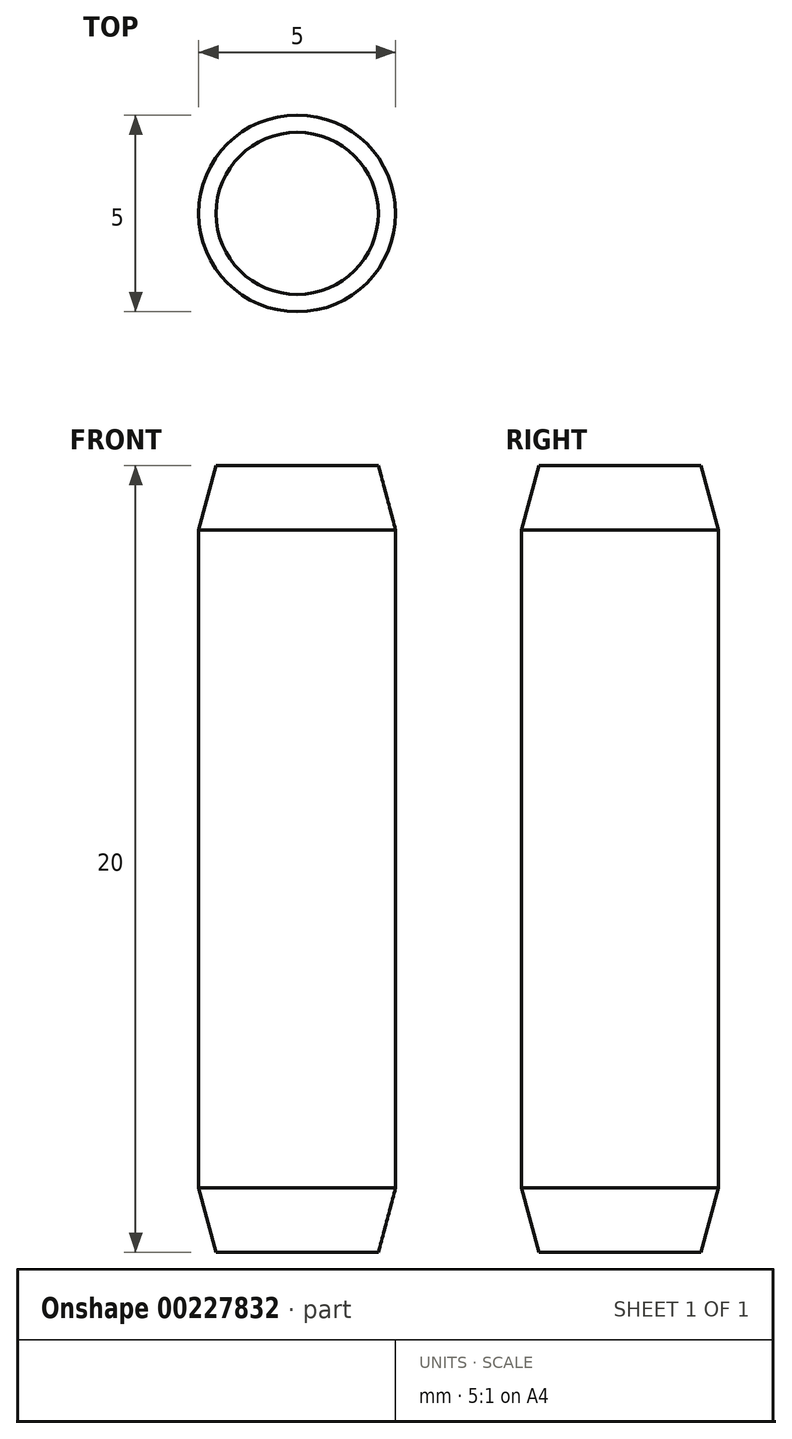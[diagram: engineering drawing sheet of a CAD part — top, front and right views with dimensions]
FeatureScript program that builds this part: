
annotation { "Feature Type Name" : "Feature", "Feature Type Description" : "" }
export const myFeature = defineFeature(function(context is Context, id is Id, definition is map)
    precondition{}
    {
        {
            var Q0;
            Q0=qCreatedBy(makeId("Front.planeOp"),FACE);
            var sketch = newSketch(context, id + "F0", { "sketchPlane" : qUnion([Q0])});
            skLineSegment(sketch, "E0", {"start": v(-2.06, 10) * mm, "end": v(-2.5, 8.36) * mm});
            skLineSegment(sketch, "E1", {"start": v(-2.5, 8.36) * mm, "end": v(-2.5, -8.36) * mm});
            skLineSegment(sketch, "E2.MirrorCS", {"start": v(-2.06, -10) * mm, "end": v(-2.5, -8.36) * mm});
            skPoint(sketch, "E3.orphan", {"position": v(-2.5, 0) * mm});
            skLineSegment(sketch, "E4", {"start": v(-2.06, 10) * mm, "end": v(0, 10) * mm});
            skLineSegment(sketch, "E5", {"start": v(-2.06, -10) * mm, "end": v(0, -10) * mm});
            skLineSegment(sketch, "E6", {"start": v(0, 10) * mm, "end": v(0, -10) * mm});
            skSolve(sketch);
        }
        {
            var Q0;
            Q0 = qSketchRegion(id + "F0", true);
            var Q1;
            Q1=sQuery(id+"F0.wireOp",EDGE,"E6");
            revolve(context, id + "F1", {"entities" : qUnion([Q0]), "axis" : qUnion([Q1]), "revolveType" : RevolveType.FULL});
        }
    });
